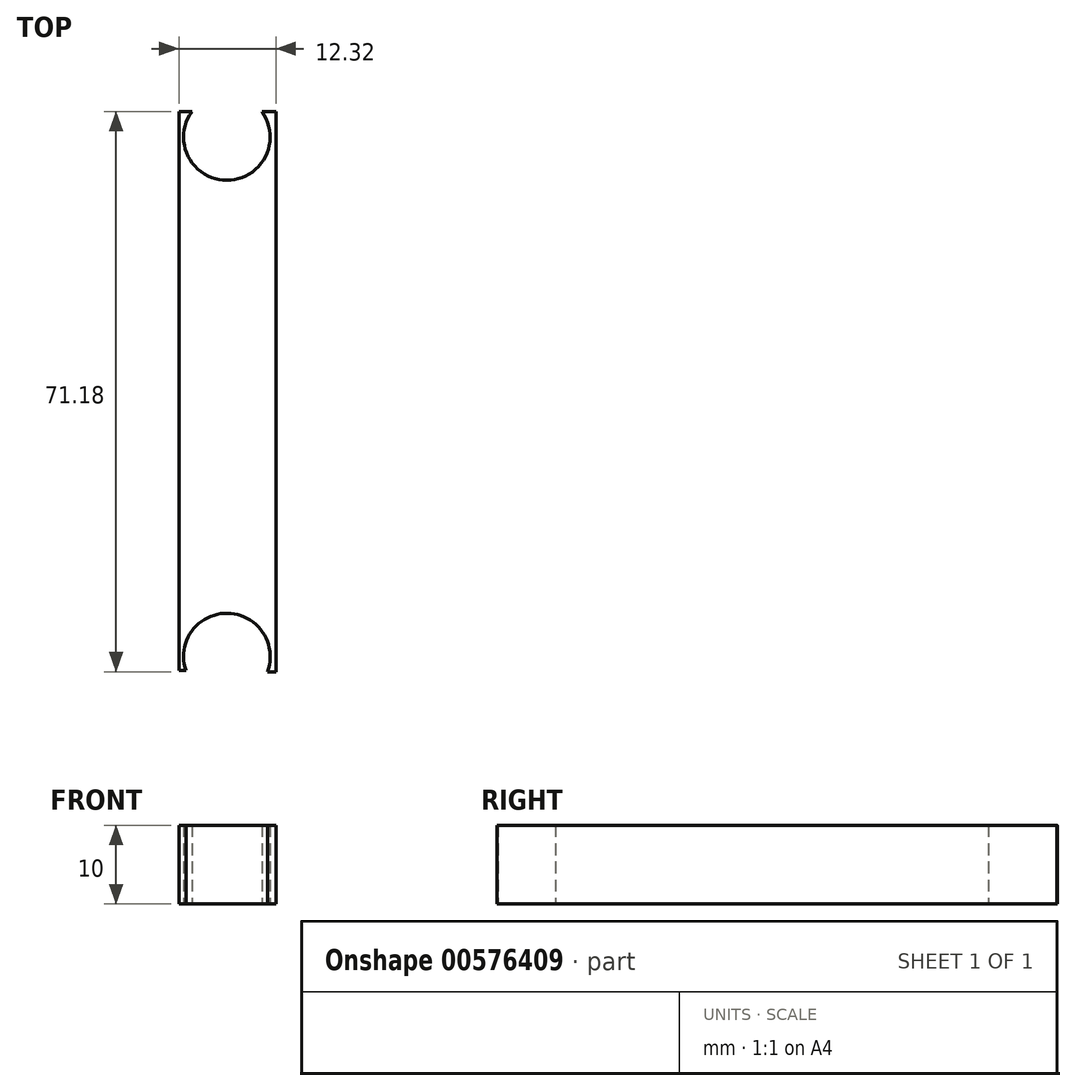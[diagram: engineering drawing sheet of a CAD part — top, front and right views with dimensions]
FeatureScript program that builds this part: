
annotation { "Feature Type Name" : "Feature", "Feature Type Description" : "" }
export const myFeature = defineFeature(function(context is Context, id is Id, definition is map)
    precondition{}
    {
        {
            var Q0;
            Q0=qCreatedBy(makeId("Top.planeOp"),FACE);
            var sketch = newSketch(context, id + "F0", { "sketchPlane" : qUnion([Q0])});
            skLineSegment(sketch, "E0", {"start": v(0, 0) * mm, "end": v(0, 33) * mm});
            skLineSegment(sketch, "E1", {"start": v(0, 0) * mm, "end": v(0, -33) * mm});
            skLineSegment(sketch, "E2.bottom", {"start": v(0, 27) * mm, "end": v(0, 27) * mm});
            skLineSegment(sketch, "E2.top", {"start": v(0, -27) * mm, "end": v(0, -27) * mm});
            skLineSegment(sketch, "E3.bottom", {"start": v(21.5, 21.5) * mm, "end": v(21.48, 21.5) * mm});
            skPoint(sketch, "E3.middle", {"position": v(0, 0) * mm});
            skCircle(sketch, "E4", {"center": v(0, 33) * mm, "radius": 5.5 * mm});
            skCircle(sketch, "E5", {"center": v(0, -33) * mm, "radius": 5.5 * mm});
            skPoint(sketch, "E6.visualSharp", {"position": v(50.3, 44.06) * mm});
            skLineSegment(sketch, "E7", {"start": v(0, 0) * mm, "end": v(-12, 0) * mm, "construction": true});
            skLineSegment(sketch, "E8", {"start": v(-6.05, 36.24) * mm, "end": v(-6.08, -34.78) * mm});
            skLineSegment(sketch, "E9", {"start": v(-6.08, -34.78) * mm, "end": v(6.24, -34.94) * mm});
            skLineSegment(sketch, "E10", {"start": v(-6.05, 36.24) * mm, "end": v(6.24, 36.21) * mm});
            skLineSegment(sketch, "E11", {"start": v(6.24, -34.94) * mm, "end": v(6.24, 36.21) * mm});
            skSolve(sketch);
        }
        {
            var Q0;
            {var subQ10=sQuery(id+"F0.wireOp",EDGE,"E11");Q0=makeQuery(id+"F0.imprint","IMPRINT",FACE,{"disambiguationData":[TD([[makeQuery(id+"F0.imprint","IMPRINT",EDGE,{"derivedFrom":subQ10}),1.0]])]});}
            var Q1;
            {var subQ9=sQuery(id+"F0.wireOp",EDGE,"E8");Q1=makeQuery(id+"F0.imprint","IMPRINT",FACE,{"disambiguationData":[TD([[makeQuery(id+"F0.imprint","IMPRINT",EDGE,{"derivedFrom":subQ9}),1.0]])]});}
            extrude(context, id + "F1", {"entities" : qUnion([Q0, Q1]), "depth" : 10 * mm, "offsetDistance" : 25 * mm});
        }
    });
